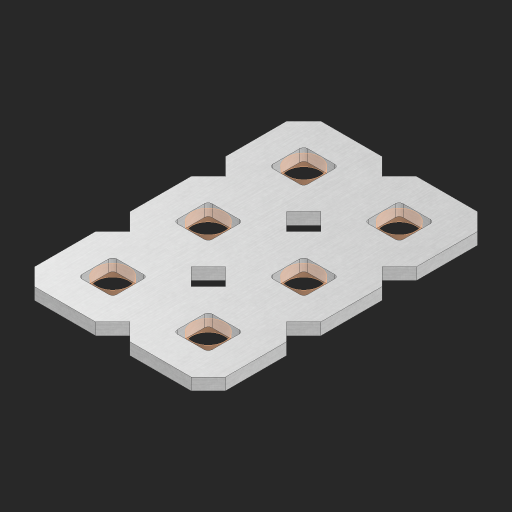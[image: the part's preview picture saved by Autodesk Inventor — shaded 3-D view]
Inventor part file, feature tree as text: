
AUTODESK INVENTOR PART (.ipt)
format: ipt  version: 2023 (Build 270158000, 158)  size: 361,984 bytes
history: native  units: in
note: dims shown in document units (in); Inventor stores cm internally (conversion verified against a paired STEP export)
features: other x7, extrude x5, sketch x2, pattern_linear x1
ambient origin geometry x8: Origin, YZ Plane, XZ Plane, XY Plane, X Axis, Y Axis, Z Axis, Center Point
bodies: Solid1 (feature_tree), Body (feature_tree)
feature tree (15):
  pattern_linear  "Rectangular Pattern1"  Spacing1=0.09in  [1 undecoded]
  sketch  "Sketch1"  dims[d1=0.5in]
  sketch  "Sketch2"  dims[d2=0.182in d3=0.09in d4=0.09in d5=0.09in d6=0.09in d7=0.09in d8=0.09in d9=0.09in d10=0.09in d11=0.02in d13=0.0in d14=0.172in d15=0.0625in d16=0.0in d19=0.5in d22=0.5in]
  other  "Srf1"
  other  "Srf126"
  other  "Srf127"
  other  "Srf268"
  other  "Srf269"
  other  "Srf270"
  other  "Circle"
  extrude  "ExtrusionSrf126"  Depth=0.09in
  extrude  "ExtrusionSrf127"  Depth=0.09in
  extrude  "ExtrusionSrf268"  Depth=0.09in
  extrude  "ExtrusionSrf269"  Depth=0.09in
  extrude  "ExtrusionSrf270"  Depth=0.09in
note: 1 required parameter value undecoded (feature->parameter linkage not recoverable at this tier; creation-order binding heuristic only, values carry confidence <= 0.55)
